# Revit family: Kanalhalter LLN, VA
name_source: partatom
category: Allgemeines Modell
revit_build: Autodesk Revit 2017 (Build: 20190507_1515(x64)
units: mm (PartAtom-declared; Revit-internal decimal feet)

## family parameters
Arbeitsebenenbasiert = Ja
Beim Laden mit Abzugskörper schneiden = Nein
Bemaßung runder Anschluss = Durchmesser verwenden
Gemeinsam genutzt = Ja
Immer vertikal = Nein
Kann Basisbauteil für Bewehrung sein = Nein
Raumberechnungspunkt = Nein
Teiletyp = Normal

## types (2) — shared parameters
Anschluss = M8/M10
Ausführung = leicht
Bauart = L
Breite Material = 30 mm
Dämmelementtyp = genietet
Fabrikat = MEFA
Firma = MEFA Befestigungs- und Montagesysteme GmbH
Gewicht = 0.11 kg
Gewicht pro Bauteil = 0.11 kg
Höhe = 90 mm
Kurztext2 = Höhe 90 mm Gummi genietet
Länge = 40 mm  [stored 0.131234 ft]
Mengeneinheit = St
Schalldämmeinlage = Gummi SBR
Stärke Material = 3 mm  [stored 0.00984252 ft]
Vorgabe-Ansicht = 1219 mm
max. Temperaturbeständigkeit = 100 °C
max. zul. Last hängend = 0.00 kN
max. zul. Last stehend = 0.90 kN
vpe = 1 St

## per-type parameters (varying)
| type | Artikelnummer | EAN | Kanalhalterwinkel L VA | Kurztext1 | Unterlegscheibe VA |
| Kanalhalter LLN, V2A | 0590003 | 4250928414946 | Kanalhalterwinkel L VA : MEFA Kanalhalterwinkel L V2A (8469831) | Kanalhalter L V2A | Unterlegscheibe VA : Unterlegscheibe 13,0x24x2,5 V2A |
| Kanalhalter LLN, V4A | 0590004 | 4250928414953 | Kanalhalterwinkel L VA : MEFA Kanalhalterwinkel L V4A (8459831) | Kanalhalter L V4A | Unterlegscheibe VA : Unterlegscheibe 13,0x24x2,5 V4A |

note: [stored X ft] marks values corroborated as IEEE doubles in the binary element streams (Revit-internal decimal feet)
